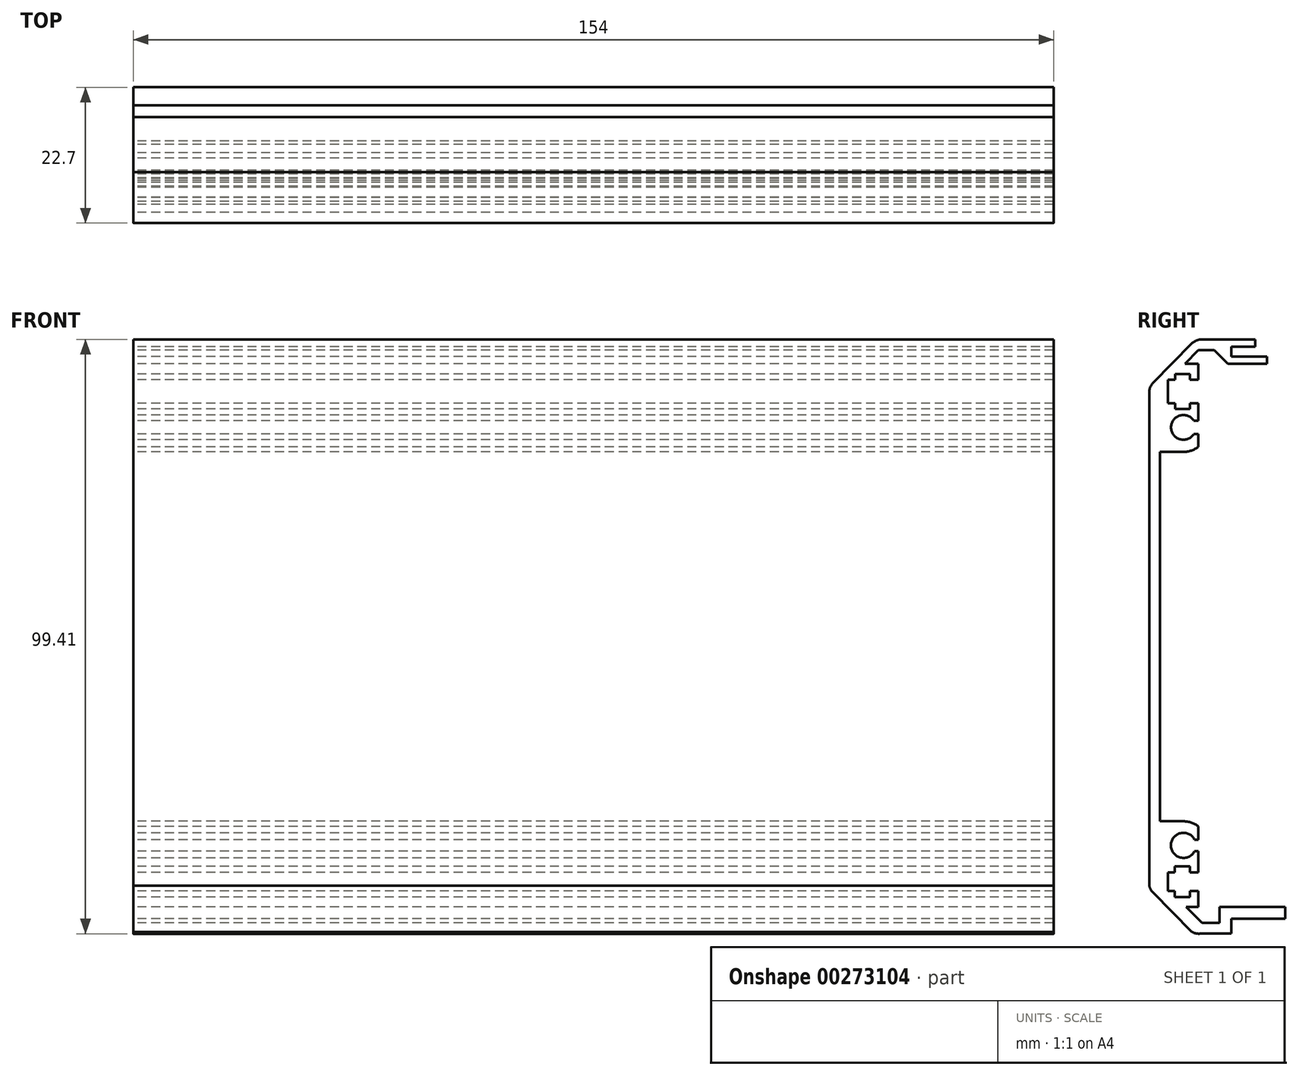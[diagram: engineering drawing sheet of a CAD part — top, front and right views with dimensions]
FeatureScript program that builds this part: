
annotation { "Feature Type Name" : "Feature", "Feature Type Description" : "" }
export const myFeature = defineFeature(function(context is Context, id is Id, definition is map)
    precondition{}
    {
        {
            var Q0;
            Q0=qCreatedBy(makeId("Right.planeOp"),FACE);
            var sketch = newSketch(context, id + "F0", { "sketchPlane" : qUnion([Q0])});
            skLineSegment(sketch, "E0", {"start": v(-56.8, 86.52) * mm, "end": v(-52.8, 86.52) * mm});
            skLineSegment(sketch, "E1", {"start": v(-61.98, 87.72) * mm, "end": v(-52.8, 87.72) * mm});
            skLineSegment(sketch, "E2", {"start": v(-70.5, 78.99) * mm, "end": v(-70.5, -2.97) * mm});
            skLineSegment(sketch, "E3", {"start": v(-56.8, -11.68) * mm, "end": v(-56.8, -9.18) * mm});
            skLineSegment(sketch, "E4", {"start": v(-52.8, 87.72) * mm, "end": v(-52.8, 86.52) * mm});
            skLineSegment(sketch, "E5", {"start": v(-56.8, -9.18) * mm, "end": v(-47.8, -9.18) * mm});
            skLineSegment(sketch, "E6", {"start": v(-47.8, -9.18) * mm, "end": v(-47.8, -7.18) * mm});
            skLineSegment(sketch, "E7", {"start": v(-68.7, 7.12) * mm, "end": v(-64.8, 7.12) * mm});
            skLineSegment(sketch, "E8", {"start": v(-64.8, 68.92) * mm, "end": v(-68.7, 68.92) * mm});
            skLineSegment(sketch, "E9", {"start": v(-69.91, 80.4) * mm, "end": v(-63.37, 87.06) * mm});
            skArc(sketch, "E10", {"start": v(-70.5, 78.99) * mm, "mid": v(-70.35, 79.75) * mm, "end": v(-69.91, 80.4) * mm});
            skArc(sketch, "E11", {"start": v(-63.37, 87.06) * mm, "mid": v(-62.73, 87.52) * mm, "end": v(-61.98, 87.72) * mm});
            skLineSegment(sketch, "E12", {"start": v(-56.8, -11.68) * mm, "end": v(-61.98, -11.68) * mm});
            skArc(sketch, "E13", {"start": v(-63.4, -11.39) * mm, "mid": v(-62.71, -11.64) * mm, "end": v(-61.98, -11.68) * mm});
            skLineSegment(sketch, "E14", {"start": v(-63.4, -11.39) * mm, "end": v(-69.91, -4.76) * mm});
            skLineSegment(sketch, "E15", {"start": v(-70.5, -2.97) * mm, "end": v(-70.5, -3.68) * mm});
            skArc(sketch, "E16", {"start": v(-69.91, -4.76) * mm, "mid": v(-70.28, -4.26) * mm, "end": v(-70.5, -3.68) * mm});
            skLineSegment(sketch, "E17", {"start": v(-56.8, 86.52) * mm, "end": v(-56.8, 84.87) * mm});
            skLineSegment(sketch, "E18", {"start": v(-56.8, 84.87) * mm, "end": v(-50.8, 84.87) * mm});
            skLineSegment(sketch, "E19", {"start": v(-50.8, 84.87) * mm, "end": v(-50.8, 83.67) * mm});
            skLineSegment(sketch, "E20", {"start": v(-68.7, 68.92) * mm, "end": v(-68.7, 7.12) * mm});
            skLineSegment(sketch, "E21", {"start": v(-59.63, 85.92) * mm, "end": v(-62.3, 85.92) * mm});
            skLineSegment(sketch, "E22", {"start": v(-62.3, 85.92) * mm, "end": v(-64.51, 83.67) * mm});
            skLineSegment(sketch, "E23", {"start": v(-64.51, 83.67) * mm, "end": v(-62.3, 83.67) * mm});
            skLineSegment(sketch, "E24", {"start": v(-59.63, 85.92) * mm, "end": v(-57.37, 83.67) * mm});
            skLineSegment(sketch, "E25", {"start": v(-50.8, 83.67) * mm, "end": v(-57.37, 83.67) * mm});
            skLineSegment(sketch, "E26", {"start": v(-50.8, 79.02) * mm, "end": v(-86.58, 79.02) * mm, "construction": true});
            skArc(sketch, "E27", {"start": v(-64.8, 68.92) * mm, "mid": v(-63.48, 69.14) * mm, "end": v(-62.3, 69.77) * mm});
            skLineSegment(sketch, "E28.left", {"start": v(-67.42, 80.98) * mm, "end": v(-67.42, 77.06) * mm});
            skPoint(sketch, "E28.middle", {"position": v(-62.3, 79.02) * mm});
            skLineSegment(sketch, "E29", {"start": v(-62.3, 83.67) * mm, "end": v(-62.3, 80.98) * mm});
            skLineSegment(sketch, "E30", {"start": v(-62.3, 74.15) * mm, "end": v(-63.07, 74.15) * mm});
            skArc(sketch, "E31", {"start": v(-63.07, 74.15) * mm, "mid": v(-66.86, 73.02) * mm, "end": v(-63.07, 71.9) * mm});
            skLineSegment(sketch, "E32", {"start": v(-63.07, 71.9) * mm, "end": v(-62.3, 71.9) * mm});
            skLineSegment(sketch, "E33", {"start": v(-62.3, 69.77) * mm, "end": v(-62.3, 71.9) * mm});
            skLineSegment(sketch, "E34", {"start": v(-62.3, 74.15) * mm, "end": v(-62.3, 77.06) * mm});
            skLineSegment(sketch, "E35.bottom", {"start": v(-66.2, 81.96) * mm, "end": v(-63.7, 81.96) * mm});
            skLineSegment(sketch, "E35.top", {"start": v(-66.2, 76.09) * mm, "end": v(-63.7, 76.09) * mm});
            skPoint(sketch, "E35.middle", {"position": v(-64.95, 79.02) * mm});
            skLineSegment(sketch, "E36", {"start": v(-62.3, 80.98) * mm, "end": v(-63.7, 80.98) * mm});
            skLineSegment(sketch, "E37", {"start": v(-67.42, 80.98) * mm, "end": v(-66.2, 80.98) * mm});
            skLineSegment(sketch, "E38", {"start": v(-67.42, 77.06) * mm, "end": v(-66.2, 77.06) * mm});
            skLineSegment(sketch, "E39", {"start": v(-62.3, 77.06) * mm, "end": v(-63.7, 77.06) * mm});
            skLineSegment(sketch, "E40", {"start": v(-63.7, 80.98) * mm, "end": v(-63.7, 81.96) * mm});
            skLineSegment(sketch, "E41", {"start": v(-66.2, 81.96) * mm, "end": v(-66.2, 80.98) * mm});
            skLineSegment(sketch, "E42", {"start": v(-66.2, 76.09) * mm, "end": v(-66.2, 77.06) * mm});
            skLineSegment(sketch, "E43", {"start": v(-63.7, 77.06) * mm, "end": v(-63.7, 76.09) * mm});
            skArc(sketch, "E44", {"start": v(-64.8, 7.12) * mm, "mid": v(-63.47, 6.9) * mm, "end": v(-62.3, 6.25) * mm});
            skPoint(sketch, "E45.middle", {"position": v(-62.3, 3.1) * mm});
            skLineSegment(sketch, "E46", {"start": v(-62.3, 4.04) * mm, "end": v(-62.3, 6.25) * mm});
            skArc(sketch, "E47", {"start": v(-62.92, 4.04) * mm, "mid": v(-66.9, 3.1) * mm, "end": v(-62.92, 2.15) * mm});
            skLineSegment(sketch, "E48", {"start": v(-62.3, 4.04) * mm, "end": v(-62.92, 4.04) * mm});
            skLineSegment(sketch, "E49", {"start": v(-62.3, 2.15) * mm, "end": v(-62.92, 2.15) * mm});
            skLineSegment(sketch, "E50", {"start": v(-45.84, -2.98) * mm, "end": v(-85.2, -2.98) * mm, "construction": true});
            skLineSegment(sketch, "E51", {"start": v(-58.76, -7.18) * mm, "end": v(-58.76, -9.86) * mm});
            skLineSegment(sketch, "E52", {"start": v(-58.76, -9.86) * mm, "end": v(-61.7, -9.86) * mm});
            skLineSegment(sketch, "E53", {"start": v(-61.7, -9.86) * mm, "end": v(-64.34, -7.18) * mm});
            skLineSegment(sketch, "E54", {"start": v(-64.34, -7.18) * mm, "end": v(-62.3, -7.18) * mm});
            skLineSegment(sketch, "E55", {"start": v(-47.8, -7.18) * mm, "end": v(-58.76, -7.18) * mm});
            skLineSegment(sketch, "E56.left", {"start": v(-67.42, -1.4) * mm, "end": v(-67.42, -4.55) * mm});
            skPoint(sketch, "E56.middle", {"position": v(-62.2, -2.98) * mm});
            skLineSegment(sketch, "E57", {"start": v(-62.3, 2.15) * mm, "end": v(-62.3, -1.4) * mm});
            skLineSegment(sketch, "E58", {"start": v(-62.3, -7.18) * mm, "end": v(-62.3, -4.55) * mm});
            skPoint(sketch, "E58.endSnap0", {"position": v(-62.2, -4.55) * mm});
            skLineSegment(sketch, "E59.bottom", {"start": v(-66.26, -0.42) * mm, "end": v(-63.7, -0.42) * mm});
            skLineSegment(sketch, "E59.top", {"start": v(-66.26, -5.53) * mm, "end": v(-63.7, -5.53) * mm});
            skPoint(sketch, "E59.middle", {"position": v(-64.97, -2.98) * mm});
            skLineSegment(sketch, "E60", {"start": v(-62.3, -1.4) * mm, "end": v(-63.7, -1.4) * mm});
            skLineSegment(sketch, "E61", {"start": v(-67.42, -1.4) * mm, "end": v(-66.26, -1.4) * mm});
            skLineSegment(sketch, "E62", {"start": v(-67.42, -4.55) * mm, "end": v(-66.26, -4.55) * mm});
            skLineSegment(sketch, "E63", {"start": v(-62.3, -4.55) * mm, "end": v(-63.7, -4.55) * mm});
            skLineSegment(sketch, "E64", {"start": v(-66.26, -4.55) * mm, "end": v(-66.26, -5.53) * mm});
            skLineSegment(sketch, "E65", {"start": v(-63.7, -5.53) * mm, "end": v(-63.7, -4.55) * mm});
            skLineSegment(sketch, "E66", {"start": v(-66.26, -1.4) * mm, "end": v(-66.26, -0.42) * mm});
            skLineSegment(sketch, "E67", {"start": v(-63.7, -0.42) * mm, "end": v(-63.7, -1.4) * mm});
            skSolve(sketch);
        }
        {
            var Q0;
            Q0=qSketchRegion(id+"F0",true);
            extrude(context, id + "F1", {"entities" : qUnion([Q0]), "flatOperationType" : FlatOperationType.REMOVE, "offsetDistance" : 25 * mm, "depth" : 154 * mm, "domain" : OperationDomain.MODEL});
        }
    });
